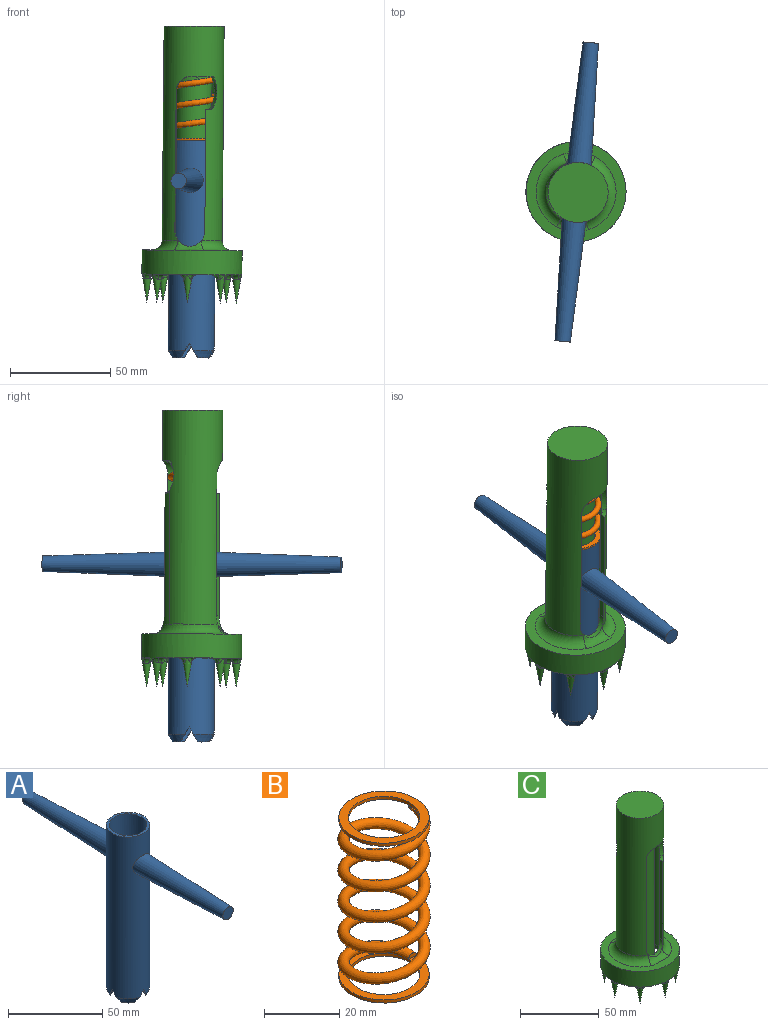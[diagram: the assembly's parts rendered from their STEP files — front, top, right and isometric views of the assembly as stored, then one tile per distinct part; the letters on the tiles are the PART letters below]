
ASSEMBLY  parts=3 mates=2
PART A: 19 faces, bbox 23x150x108.8 mm
  f0: cylinder r=10mm len=108.75mm, axis (0,0,-1), area 6704.1mm2, adj f2,f3,f4,f5,f6,f7,f8,f9
  f1: cylinder r=11.5mm len=105mm, axis (0,0,-1), area 7310.1mm2, adj f2,f3,f4,f5,f6,f7,f8,f9
  f2: plane 23x23mm, normal (0,0,1), area 101.3mm2, adj f0,f1
  f3: plane 7.43x4.29mm, normal (0,-0.87,-0.5), area 9.8mm2, adj f0,f1,f4,f14
  f4: plane 7.43x4.29mm, normal (0,0.87,-0.5), area 9.8mm2, adj f0,f1,f3,f11
  f5: plane 7.43x4.29mm, normal (0,0.87,-0.5), area 9.8mm2, adj f0,f1,f6,f12
  f6: plane 7.43x4.29mm, normal (0,-0.87,-0.5), area 9.8mm2, adj f0,f1,f5,f13
  f7: plane 7.43x4.29mm, normal (0.87,0,-0.5), area 9.8mm2, adj f0,f1,f8,f11
  f8: plane 7.43x4.29mm, normal (-0.87,0,-0.5), area 9.8mm2, adj f0,f1,f7,f12
  f9: plane 7.43x4.29mm, normal (-0.87,0,-0.5), area 9.8mm2, adj f0,f1,f10,f13
  f10: plane 7.43x4.29mm, normal (0.87,0,-0.5), area 9.8mm2, adj f0,f1,f9,f14
  f11: cone r=11.5mm half-angle=21.8deg, axis (0,0,1), area 41.9mm2, adj f0,f1,f4,f7
  f12: cone r=11.5mm half-angle=21.8deg, axis (0,0,1), area 41.9mm2, adj f0,f1,f5,f8
  f13: cone r=11.5mm half-angle=21.8deg, axis (0,0,1), area 41.9mm2, adj f0,f1,f6,f9
  f14: cone r=11.5mm half-angle=21.8deg, axis (0,0,1), area 41.9mm2, adj f0,f1,f3,f10
  f15: plane 7.76x7.76mm, normal (0,1,0), area 47.3mm2, adj f16
  f16: cone r=6.5mm half-angle=2deg, axis (0,-1,0), area 2025.5mm2, adj f1,f15
  f17: plane 7.76x7.76mm, normal (0,-1,0), area 47.3mm2, adj f18
  f18: cone r=6.5mm half-angle=2deg, axis (0,1,0), area 2025.5mm2, adj f1,f17
PART B: 15 faces, bbox 24.5x24.5x53.1 mm
  f0: plane 6.03x1.92mm, normal (0,0,-1), area 1.1mm2, adj f3,f4,f11
  f1: plane 4.82x1.37mm, normal (0,0,1), area 0.8mm2, adj f2,f4,f8
  f2: plane 3x1.5mm, normal (0,1,0), area 3.5mm2, adj f1,f4,f6,f7
  f3: plane 3x1.5mm, normal (0,-1,0), area 3.5mm2, adj f0,f4,f5,f14
  f4: bspline ~52.99x24.38mm, area 3113.1mm2, adj f0,f1,f2,f3,f5,f6,f7,f14
  f5: plane 4.84x1.38mm, normal (0,0,-1), area 0.8mm2, adj f3,f4,f12
  f6: plane 6.03x1.91mm, normal (0,0,1), area 1.1mm2, adj f2,f4,f9
  f7: plane 24x24mm, normal (0,0,-1), area 146.9mm2, adj f2,f4,f8,f9
  f8: cylinder r=9.5mm len=19mm, axis (0,0,-1), area 59.7mm2, adj f1,f7,f10
  f9: cylinder r=12mm len=24mm, axis (0,0,-1), area 75.4mm2, adj f6,f7,f10
  f10: plane 24x24mm, normal (0,0,1), area 168.9mm2, adj f8,f9
  f11: cylinder r=12mm len=24mm, axis (0,0,1), area 75.4mm2, adj f0,f13,f14
  f12: cylinder r=9.5mm len=19mm, axis (0,0,1), area 59.7mm2, adj f5,f13,f14
  f13: plane 24x24mm, normal (0,0,-1), area 168.9mm2, adj f11,f12
  f14: plane 24x24mm, normal (0,0,1), area 146.9mm2, adj f3,f4,f11,f12
PART C: 96 faces, bbox 51.7x51x138.5 mm
  f0: cylinder r=15mm len=107mm, axis (0,0,-1), area 7056.5mm2, adj f1,f2,f25,f26,f28,f29,f30,f31
  f1: cylinder r=15mm len=66.95mm, axis (0,0,-1), area 299.2mm2, adj f0,f26,f27,f40,f45
  f2: cylinder r=7.5mm len=11.12mm, axis (0,1,0), area 36.8mm2, adj f0,f23,f28,f41,f42
  f3: plane 10.07x7.85mm, normal (0,0,-1), area 40.3mm2, adj f10,f11,f66,f93
  f4: plane 10.07x7.85mm, normal (0,0,-1), area 40.3mm2, adj f10,f11,f48,f78
  f5: plane 10.07x7.85mm, normal (0,0,-1), area 40.3mm2, adj f10,f11,f51,f81
  f6: plane 10.07x7.85mm, normal (0,0,-1), area 40.3mm2, adj f10,f11,f69,f87
  f7: plane 10.07x7.85mm, normal (0,0,-1), area 40.3mm2, adj f10,f11,f60,f75
  f8: plane 10.07x7.85mm, normal (0,0,-1), area 40.3mm2, adj f10,f11,f57,f90
  f9: plane 10.07x7.85mm, normal (0,0,-1), area 40.3mm2, adj f10,f11,f54,f84
  f10: cylinder r=20mm len=40mm, axis (0,0,-1), area 1256.6mm2, adj f3,f4,f5,f6,f7,f8,f9,f12
  f11: cylinder r=25mm len=50mm, axis (0,0,-1), area 1885mm2, adj f3,f4,f5,f6,f7,f8,f9,f12
  f12: plane 10.07x7.85mm, normal (0,0,-1), area 40.3mm2, adj f10,f11,f63,f72
  f13: cone r=2.5mm half-angle=10deg, axis (0,0,1), area 88.6mm2, adj f71,f72,f73,f89,f90,f91
  f14: cone r=2.5mm half-angle=10deg, axis (0,0,1), area 87.1mm2, adj f68,f69,f70,f83,f84,f85
  f15: cone r=2.5mm half-angle=10deg, axis (0,0,1), area 88.6mm2, adj f50,f51,f52,f77,f78,f79
  f16: cone r=2.5mm half-angle=10deg, axis (0,0,1), area 87.1mm2, adj f65,f66,f67,f74,f75,f76
  f17: cone r=2.5mm half-angle=10deg, axis (0,0,1), area 85.6mm2, adj f62,f63,f64,f86,f87,f88
  f18: cone r=2.5mm half-angle=10deg, axis (0,0,1), area 85.3mm2, adj f53,f54,f55,f80,f81,f82
  f19: cone r=2.5mm half-angle=10deg, axis (0,0,1), area 85.3mm2, adj f47,f48,f49,f59,f60,f61
  f20: cone r=2.5mm half-angle=10deg, axis (0,0,1), area 85.6mm2, adj f56,f57,f58,f92,f93,f94
  f21: plane 40x40mm, normal (0,0,-1), area 765.8mm2, adj f10,f23
  f22: plane 50x50mm, normal (0,0,1), area 722.8mm2, adj f11,f43,f44,f45,f46
  f23: cylinder r=12.5mm len=112mm, axis (0,0,1), area 6003mm2, adj f2,f21,f24,f26,f27,f28,f29,f30
  f24: plane 25x25mm, normal (0,0,-1), area 236.4mm2, adj f23,f33
  f25: plane 30x30mm, normal (0,0,1), area 706.9mm2, adj f0
  f26: cylinder r=7.5mm len=15mm, axis (0,1,0), area 65.3mm2, adj f0,f1,f23,f27,f28,f46
  f27: plane 61.4x3.3mm, normal (1,0,0), area 182.4mm2, adj f1,f23,f26,f40
  f28: plane 70x2.99mm, normal (-1,0,0), area 209.3mm2, adj f0,f2,f23,f26
  f29: plane 61.35x3.31mm, normal (-1,0,0), area 182.2mm2, adj f0,f23,f32,f36
  f30: cylinder r=7.5mm len=11.12mm, axis (0,1,0), area 36.8mm2, adj f0,f23,f31,f37,f38
  f31: plane 70x2.99mm, normal (1,0,0), area 209.3mm2, adj f0,f23,f30,f32
  f32: cylinder r=7.5mm len=15mm, axis (0,1,0), area 65.3mm2, adj f0,f23,f29,f31,f43
  f33: cylinder r=9mm len=119mm, axis (0,0,1), area 6729.3mm2, adj f24,f95
  f34: plane 16x16mm, normal (0,0,-1), area 201.1mm2, adj f95
  f35: revolved ~15x4.23mm, area 43.1mm2, adj f0,f23,f36,f37
  f36: revolved ~5.33x5.08mm, area 11.1mm2, adj f0,f23,f29,f35
  f37: plane 10.15x7.07mm, normal (0,0,-1), area 24.9mm2, adj f0,f23,f30,f35,f38
  f38: plane 2.85x2.4mm, normal (0.64,-0.77,0), area 1.2mm2, adj f23,f30,f37
  f39: revolved ~15x4.23mm, area 43.1mm2, adj f0,f23,f40,f41
  f40: revolved ~5.33x5.08mm, area 10.9mm2, adj f1,f23,f27,f39
  f41: plane 10.15x7.07mm, normal (0,0,-1), area 24.9mm2, adj f0,f2,f23,f39,f42
  f42: plane 2.85x2.4mm, normal (-0.64,0.77,0), area 1.2mm2, adj f2,f23,f41
  f43: bspline ~17.22x5.78mm, area 80.2mm2, adj f22,f32,f44,f45
  f44: torus R=20mm, axis (0,0,1), area 306.2mm2, adj f0,f22,f43,f46
  f45: torus R=20mm, axis (0,0,1), area 306.2mm2, adj f0,f1,f22,f43,f46
  f46: bspline ~17.22x5.78mm, area 80.2mm2, adj f22,f26,f44,f45
  f47: bspline ~3.18x2.59mm, area 3.7mm2, adj f10,f19,f48
  f48: torus R=5.02mm, axis (0,0,1), area 14.2mm2, adj f4,f19,f47,f49
  f49: bspline ~3.68x3.03mm, area 5.6mm2, adj f11,f19,f48
  f50: bspline ~4.2x2.58mm, area 4.6mm2, adj f10,f15,f51
  f51: torus R=5.02mm, axis (0,0,1), area 14.2mm2, adj f5,f15,f50,f52
  f52: bspline ~4.75x2.6mm, area 3.7mm2, adj f11,f15,f51
  f53: bspline ~3.29x2.66mm, area 5.1mm2, adj f10,f18,f54
  f54: torus R=5.02mm, axis (0,0,1), area 14.2mm2, adj f9,f18,f53,f55
  f55: bspline ~3.68x3.03mm, area 5.6mm2, adj f11,f18,f54
  f56: bspline ~3.68x3.03mm, area 5.6mm2, adj f11,f20,f57
  f57: torus R=5.02mm, axis (0,0,1), area 14.2mm2, adj f8,f20,f56,f58
  f58: bspline ~3.18x2.59mm, area 3.7mm2, adj f10,f20,f57
  f59: bspline ~3.68x3.03mm, area 5.6mm2, adj f11,f19,f60
  f60: torus R=5.02mm, axis (0,0,1), area 14.2mm2, adj f7,f19,f59,f61
  f61: bspline ~3.29x2.66mm, area 5.1mm2, adj f10,f19,f60
  f62: bspline ~3.18x2.59mm, area 3.7mm2, adj f10,f17,f63
  f63: torus R=5.02mm, axis (0,0,1), area 14.2mm2, adj f12,f17,f62,f64
  f64: bspline ~3.68x3.03mm, area 5.6mm2, adj f11,f17,f63
  f65: bspline ~4.75x2.6mm, area 3.7mm2, adj f11,f16,f66
  f66: torus R=5.02mm, axis (0,0,1), area 14.2mm2, adj f3,f16,f65,f67
  f67: bspline ~4.2x2.58mm, area 4.6mm2, adj f10,f16,f66
  f68: bspline ~4.2x2.58mm, area 4.6mm2, adj f10,f14,f69
  f69: torus R=5.02mm, axis (0,0,1), area 14.2mm2, adj f6,f14,f68,f70
  f70: bspline ~4.75x2.6mm, area 3.7mm2, adj f11,f14,f69
  f71: bspline ~4.75x2.6mm, area 3.7mm2, adj f11,f13,f72
  f72: torus R=5.02mm, axis (0,0,1), area 14.2mm2, adj f12,f13,f71,f73
  f73: bspline ~4.2x2.58mm, area 4.6mm2, adj f10,f13,f72
  f74: bspline ~4.2x2.58mm, area 4.6mm2, adj f10,f16,f75
  f75: torus R=5.02mm, axis (0,0,1), area 14.2mm2, adj f7,f16,f74,f76
  f76: bspline ~4.75x2.6mm, area 3.7mm2, adj f11,f16,f75
  f77: bspline ~4.75x2.6mm, area 3.7mm2, adj f11,f15,f78
  f78: torus R=5.02mm, axis (0,0,1), area 14.2mm2, adj f4,f15,f77,f79
  f79: bspline ~4.2x2.58mm, area 4.6mm2, adj f10,f15,f78
  f80: bspline ~3.68x3.03mm, area 5.6mm2, adj f11,f18,f81
  f81: torus R=5.02mm, axis (0,0,1), area 14.2mm2, adj f5,f18,f80,f82
  f82: bspline ~3.18x2.59mm, area 3.7mm2, adj f10,f18,f81
  f83: bspline ~4.75x2.6mm, area 3.7mm2, adj f11,f14,f84
  f84: torus R=5.02mm, axis (0,0,1), area 14.2mm2, adj f9,f14,f83,f85
  f85: bspline ~4.2x2.58mm, area 4.6mm2, adj f10,f14,f84
  f86: bspline ~3.68x3.03mm, area 5.6mm2, adj f11,f17,f87
  f87: torus R=5.02mm, axis (0,0,1), area 14.2mm2, adj f6,f17,f86,f88
  f88: bspline ~3.18x2.59mm, area 3.7mm2, adj f10,f17,f87
  f89: bspline ~4.2x2.58mm, area 4.6mm2, adj f10,f13,f90
  f90: torus R=5.02mm, axis (0,0,1), area 14.2mm2, adj f8,f13,f89,f91
  f91: bspline ~4.75x2.6mm, area 3.7mm2, adj f11,f13,f90
  f92: bspline ~3.18x2.59mm, area 3.7mm2, adj f10,f20,f93
  f93: torus R=5.02mm, axis (0,0,1), area 14.2mm2, adj f3,f20,f92,f94
  f94: bspline ~3.68x3.03mm, area 5.6mm2, adj f11,f20,f93
  f95: torus R=8mm, axis (0,0,-1), area 85.2mm2, adj f33,f34
PLACE A rot(axis=(0.05,0.1,-0.99),5.4deg) t=(-29.54,-84.42,-113.17)mm
PLACE B rot(axis=(0.05,0.1,-0.99),5.4deg) t=(-28.54,-84.96,-2.18)mm
PLACE C rot(axis=(0.05,0.1,-0.99),5.4deg) t=(-29.15,-84.63,-70.18)mm fixed
MATE cylindrical B.f11 <-> C.f11  axis (-0.01,0,-1) through (-28.55,-84.95,-3.18)mm
MATE fastened B.f11 <-> A.f1  axis (-0.01,0,-1) through (-28.55,-84.95,-3.18)mm
